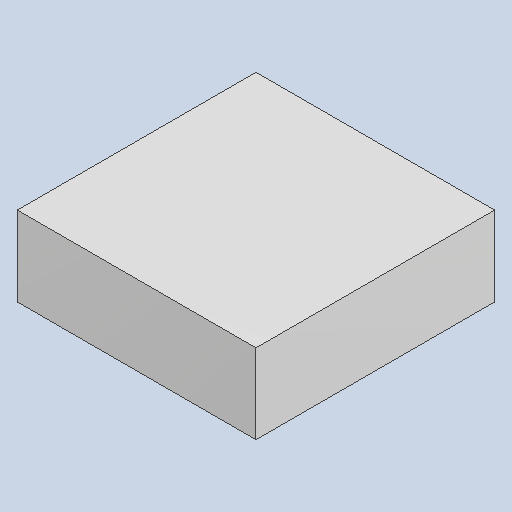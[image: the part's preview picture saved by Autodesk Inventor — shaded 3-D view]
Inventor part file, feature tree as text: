
AUTODESK INVENTOR PART (.ipt)
format: ipt  version: 2023.4 (Build 274418000, 418)  size: 79,872 bytes
history: native  units: mm
features: extrude x1
ambient origin geometry x8: Origin, YZ Plane, XZ Plane, XY Plane, X Axis, Y Axis, Z Axis, Center Point
bodies: Solid1 (feature_tree)
feature tree (1):
  extrude  "Extruded_53"  [1 undecoded]
note: 1 required parameter value undecoded (feature->parameter linkage not recoverable at this tier; creation-order binding heuristic only, values carry confidence <= 0.55)
